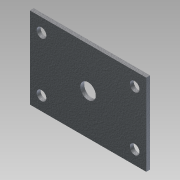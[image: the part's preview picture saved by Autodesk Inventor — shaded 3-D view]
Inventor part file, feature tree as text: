
AUTODESK INVENTOR PART (.ipt)
format: ipt  version: 2012 (Build 160160000, 160)  size: 114,688 bytes
history: native  units: in
note: dims shown in document units (in); Inventor stores cm internally (conversion verified against a paired STEP export)
features: extrude x3, sketch x3
ambient origin geometry x8: Origin, YZ Plane, XZ Plane, XY Plane, X Axis, Y Axis, Z Axis, Center Point
bodies: Solid1 (feature_tree)
feature tree (6):
  extrude  "Extrusion1"  Depth=3.75in
  extrude  "Extrusion2"  Depth=0.875in
  extrude  "Extrusion3"  Depth=0.875in
  sketch  "Sketch1"  dims[d0=2.625in d1=3.75in]
  sketch  "Sketch2"  dims[d2=0.125in d3=0.0in d4=0.875in]
  sketch  "Sketch3"  dims[d5=1.5in d6=0.875in d7=1.5in d8=0.3125in d9=0.3125in d10=0.3125in d11=0.3125in d12=0.125in d13=0.0in d14=0.5in d15=0.125in d16=0.0in]
